# Revit family: 90000951
name_source: partatom
category: Mechanical Equipment
units: mm (PartAtom-declared; Revit-internal decimal feet)

## family parameters
Cut with Voids When Loaded = No
Host = Face
Maintain Annotation Orientation = No
OmniClass Number = 23.70.50.11
OmniClass Title = Pumps for Liquid Waste
Part Type = Normal
Room Calculation Point = No
Round Connector Dimension = Use Diameter
Shared = No

## types (1)
- 90000951
    Assembly Code = MINI-ORANGE PUMP
    AssetType = Fixed
    ClassificationName = Uniclass2015
    ClassificationValue = Pr_65_53_86_05
    Color = Orange
    Default Elevation = 1219 mm
    Description = SILENT+ MINI ORANGE CONDENSATE PUMP
    DurationUnit = Year
    ExpectedLife = 0
    Export Type to IFC As = IfcPump
    IfcExportAs = IfcPump
    IfcExportType = IfcPumpType
    Keynote = R
    Manufacturer = Airflow Developments
    ManufacturerName = Airflow Developments
    Model = Silent Mini Orange Condensate Pump
    ModelNumber = FP3313
    ModelReference = Silent Mini Orange Condensate Pump
    NBSReference = 90-20-75/400
    NominalDepth = 39 mm  [stored 0.127953 ft]
    NominalHeight = 51 mm
    NominalLength = 116 mm  [stored 0.380577 ft]
    ProductionYear = 2017
    Shape = Rectangle
    Size = 116x39x51mm / 80x39x34mm
    Type Comments = FP3313
    Type IFC Predefined Type = IfcPumpType
    URL = https://www.airflow.com
    WarrantyDurationUnit = Year
    _BSBibleVersion = 14
    _BimSpecGuid = 0
    _CurrentRevision = 1

note: [stored X ft] marks values corroborated as IEEE doubles in the binary element streams (Revit-internal decimal feet)

## geometry (parser evidence)
native form markers: Sweep x1
no freeform markers — native parametric forms only
